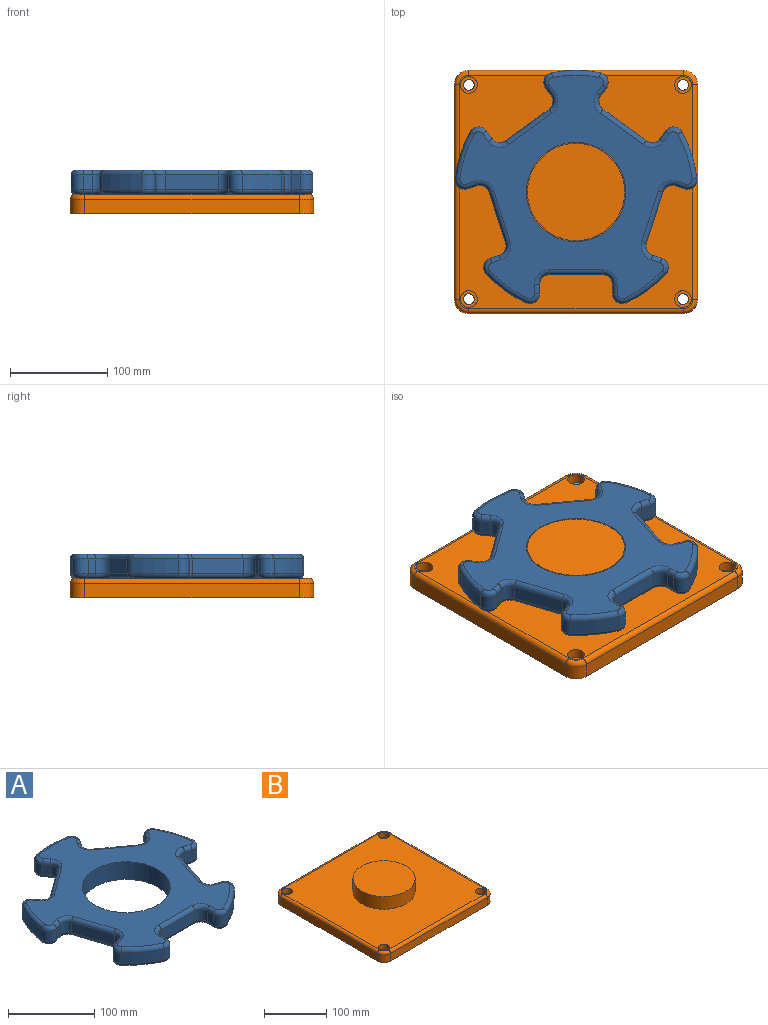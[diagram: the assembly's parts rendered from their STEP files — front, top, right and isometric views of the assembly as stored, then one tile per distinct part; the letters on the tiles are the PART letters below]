
ASSEMBLY  parts=2 mates=1
PART A: 123 faces, bbox 268.9x258.5x25 mm
  f0: plane 238.57x229.73mm, normal (0,0,1), area 21505.7mm2, adj f6,f43,f44,f45,f46,f47,f48,f49
  f1: plane 238.57x229.73mm, normal (0,0,-1), area 21505.7mm2, adj f6,f83,f84,f85,f86,f87,f88,f89
  f2: cylinder r=125mm len=40.68mm, axis (0,0,-1), area 759.5mm2, adj f13,f42,f51,f91
  f3: cylinder r=125mm len=47.82mm, axis (0,0,-1), area 759.5mm2, adj f35,f41,f67,f107
  f4: cylinder r=125mm len=50.29mm, axis (0,0,-1), area 759.5mm2, adj f28,f34,f82,f122
  f5: cylinder r=125mm len=47.82mm, axis (0,0,-1), area 759.5mm2, adj f21,f27,f66,f106
  f6: cylinder r=51mm len=102mm, axis (0,0,-1), area 8011.1mm2, adj f0,f1
  f7: cylinder r=125mm len=40.68mm, axis (0,0,-1), area 759.5mm2, adj f14,f20,f50,f90
  f8: plane 15x9.73mm, normal (-1,0,0), area 146mm2, adj f11,f14,f46,f86
  f9: plane 55x15mm, normal (0,-1,0), area 825mm2, adj f11,f12,f43,f83
  f10: plane 15x9.73mm, normal (1,0,0), area 146mm2, adj f12,f13,f47,f87
  f11: cylinder r=10mm len=15mm, axis (0,0,-1), area 235.6mm2, adj f8,f9,f44,f84
  f12: cylinder r=10mm len=15mm, axis (0,0,-1), area 235.6mm2, adj f9,f10,f45,f85
  f13: cylinder r=10mm len=15mm, axis (0,0,-1), area 299.5mm2, adj f2,f10,f49,f89
  f14: cylinder r=10mm len=15mm, axis (0,0,-1), area 299.5mm2, adj f7,f8,f48,f88
  f15: plane 15x9.26mm, normal (-0.31,-0.95,0), area 146mm2, adj f18,f21,f62,f102
  f16: plane 52.31x17mm, normal (0.95,-0.31,0), area 825mm2, adj f18,f19,f58,f98
  f17: plane 15x9.26mm, normal (0.31,0.95,0), area 146mm2, adj f19,f20,f54,f94
  f18: cylinder r=10mm len=15mm, axis (0,0,-1), area 235.6mm2, adj f15,f16,f60,f100
  f19: cylinder r=10mm len=15mm, axis (0,0,-1), area 235.6mm2, adj f16,f17,f56,f96
  f20: cylinder r=10mm len=16.25mm, axis (0,0,-1), area 299.5mm2, adj f7,f17,f52,f92
  f21: cylinder r=10mm len=15mm, axis (0,0,-1), area 299.5mm2, adj f5,f15,f64,f104
  f22: plane 15x7.87mm, normal (0.81,-0.59,0), area 146mm2, adj f25,f28,f78,f118
  f23: plane 44.5x32.33mm, normal (0.59,0.81,0), area 825mm2, adj f25,f26,f74,f114
  f24: plane 15x7.87mm, normal (-0.81,0.59,0), area 146mm2, adj f26,f27,f70,f110
  f25: cylinder r=10mm len=15mm, axis (0,0,-1), area 235.6mm2, adj f22,f23,f76,f116
  f26: cylinder r=10mm len=15mm, axis (0,0,-1), area 235.6mm2, adj f23,f24,f72,f112
  f27: cylinder r=10mm len=16.78mm, axis (0,0,-1), area 299.5mm2, adj f5,f24,f68,f108
  f28: cylinder r=10mm len=15.67mm, axis (0,0,-1), area 299.5mm2, adj f4,f22,f80,f120
  f29: plane 15x7.87mm, normal (0.81,0.59,0), area 146mm2, adj f32,f35,f71,f111
  f30: plane 44.5x32.33mm, normal (-0.59,0.81,0), area 825mm2, adj f32,f33,f75,f115
  f31: plane 15x7.87mm, normal (-0.81,-0.59,0), area 146mm2, adj f33,f34,f79,f119
  f32: cylinder r=10mm len=15mm, axis (0,0,-1), area 235.6mm2, adj f29,f30,f73,f113
  f33: cylinder r=10mm len=15mm, axis (0,0,-1), area 235.6mm2, adj f30,f31,f77,f117
  f34: cylinder r=10mm len=15.67mm, axis (0,0,-1), area 299.5mm2, adj f4,f31,f81,f121
  f35: cylinder r=10mm len=16.78mm, axis (0,0,-1), area 299.5mm2, adj f3,f29,f69,f109
  f36: plane 15x9.26mm, normal (-0.31,0.95,0), area 146mm2, adj f39,f42,f55,f95
  f37: plane 52.31x17mm, normal (-0.95,-0.31,0), area 825mm2, adj f39,f40,f59,f99
  f38: plane 15x9.26mm, normal (0.31,-0.95,0), area 146mm2, adj f40,f41,f63,f103
  f39: cylinder r=10mm len=15mm, axis (0,0,-1), area 235.6mm2, adj f36,f37,f57,f97
  f40: cylinder r=10mm len=15mm, axis (0,0,-1), area 235.6mm2, adj f37,f38,f61,f101
  f41: cylinder r=10mm len=15mm, axis (0,0,-1), area 299.5mm2, adj f3,f38,f65,f105
  f42: cylinder r=10mm len=16.25mm, axis (0,0,-1), area 299.5mm2, adj f2,f36,f53,f93
  f43: cylinder r=5mm len=55mm, axis (1,0,0), area 432mm2, adj f0,f9,f44,f45
  f44: torus R=15mm, axis (0,0,1), area 145.8mm2, adj f0,f11,f43,f46
  f45: torus R=15mm, axis (0,0,1), area 145.8mm2, adj f0,f12,f43,f47
  f46: cylinder r=5mm len=9.73mm, axis (0,-1,0), area 76.4mm2, adj f0,f8,f44,f48
  f47: cylinder r=5mm len=9.73mm, axis (0,1,0), area 76.4mm2, adj f0,f10,f45,f49
  f48: torus R=5mm, axis (0,0,1), area 128.3mm2, adj f0,f14,f46,f50
  f49: torus R=5mm, axis (0,0,1), area 128.3mm2, adj f0,f13,f47,f51
  f50: torus R=120mm, axis (0,0,1), area 391.9mm2, adj f0,f7,f48,f52
  f51: torus R=120mm, axis (0,0,1), area 391.9mm2, adj f0,f2,f49,f53
  f52: torus R=5mm, axis (0,0,1), area 128.3mm2, adj f0,f20,f50,f54
  f53: torus R=5mm, axis (0,0,1), area 128.3mm2, adj f0,f42,f51,f55
  f54: cylinder r=5mm len=10.8mm, axis (-0.95,0.31,0), area 76.4mm2, adj f0,f17,f52,f56
  f55: cylinder r=5mm len=10.8mm, axis (-0.95,-0.31,0), area 76.4mm2, adj f0,f36,f53,f57
  f56: torus R=15mm, axis (0,0,1), area 145.8mm2, adj f0,f19,f54,f58
  f57: torus R=15mm, axis (0,0,1), area 145.8mm2, adj f0,f39,f55,f59
  f58: cylinder r=5mm len=53.85mm, axis (0.31,0.95,0), area 432mm2, adj f0,f16,f56,f60
  f59: cylinder r=5mm len=53.85mm, axis (0.31,-0.95,0), area 432mm2, adj f0,f37,f57,f61
  f60: torus R=15mm, axis (0,0,1), area 145.8mm2, adj f0,f18,f58,f62
  f61: torus R=15mm, axis (0,0,1), area 145.8mm2, adj f0,f40,f59,f63
  f62: cylinder r=5mm len=10.8mm, axis (0.95,-0.31,0), area 76.4mm2, adj f0,f15,f60,f64
  f63: cylinder r=5mm len=10.8mm, axis (0.95,0.31,0), area 76.4mm2, adj f0,f38,f61,f65
  f64: torus R=5mm, axis (0,0,1), area 128.3mm2, adj f0,f21,f62,f66
  f65: torus R=5mm, axis (0,0,1), area 128.3mm2, adj f0,f41,f63,f67
  f66: torus R=120mm, axis (0,0,1), area 391.9mm2, adj f0,f5,f64,f68
  f67: torus R=120mm, axis (0,0,1), area 391.9mm2, adj f0,f3,f65,f69
  f68: torus R=5mm, axis (0,0,1), area 128.3mm2, adj f0,f27,f66,f70
  f69: torus R=5mm, axis (0,0,1), area 128.3mm2, adj f0,f35,f67,f71
  f70: cylinder r=5mm len=10.81mm, axis (-0.59,-0.81,0), area 76.4mm2, adj f0,f24,f68,f72
  f71: cylinder r=5mm len=10.81mm, axis (-0.59,0.81,0), area 76.4mm2, adj f0,f29,f69,f73
  f72: torus R=15mm, axis (0,0,1), area 145.8mm2, adj f0,f26,f70,f74
  f73: torus R=15mm, axis (0,0,1), area 145.8mm2, adj f0,f32,f71,f75
  f74: cylinder r=5mm len=47.44mm, axis (-0.81,0.59,0), area 432mm2, adj f0,f23,f72,f76
  f75: cylinder r=5mm len=47.44mm, axis (-0.81,-0.59,0), area 432mm2, adj f0,f30,f73,f77
  f76: torus R=15mm, axis (0,0,1), area 145.8mm2, adj f0,f25,f74,f78
  f77: torus R=15mm, axis (0,0,1), area 145.8mm2, adj f0,f33,f75,f79
  f78: cylinder r=5mm len=10.81mm, axis (0.59,0.81,0), area 76.4mm2, adj f0,f22,f76,f80
  f79: cylinder r=5mm len=10.81mm, axis (0.59,-0.81,0), area 76.4mm2, adj f0,f31,f77,f81
  f80: torus R=5mm, axis (0,0,1), area 128.3mm2, adj f0,f28,f78,f82
  f81: torus R=5mm, axis (0,0,1), area 128.3mm2, adj f0,f34,f79,f82
  f82: torus R=120mm, axis (0,0,1), area 391.9mm2, adj f0,f4,f80,f81
  f83: cylinder r=5mm len=55mm, axis (-1,0,0), area 432mm2, adj f1,f9,f84,f85
  f84: torus R=15mm, axis (0,0,1), area 145.8mm2, adj f1,f11,f83,f86
  f85: torus R=15mm, axis (0,0,1), area 145.8mm2, adj f1,f12,f83,f87
  f86: cylinder r=5mm len=9.73mm, axis (0,1,0), area 76.4mm2, adj f1,f8,f84,f88
  f87: cylinder r=5mm len=9.73mm, axis (0,-1,0), area 76.4mm2, adj f1,f10,f85,f89
  f88: torus R=5mm, axis (0,0,1), area 128.3mm2, adj f1,f14,f86,f90
  f89: torus R=5mm, axis (0,0,1), area 128.3mm2, adj f1,f13,f87,f91
  f90: torus R=120mm, axis (0,0,1), area 391.9mm2, adj f1,f7,f88,f92
  f91: torus R=120mm, axis (0,0,1), area 391.9mm2, adj f1,f2,f89,f93
  f92: torus R=5mm, axis (0,0,1), area 128.3mm2, adj f1,f20,f90,f94
  f93: torus R=5mm, axis (0,0,1), area 128.3mm2, adj f1,f42,f91,f95
  f94: cylinder r=5mm len=10.8mm, axis (0.95,-0.31,0), area 76.4mm2, adj f1,f17,f92,f96
  f95: cylinder r=5mm len=10.8mm, axis (0.95,0.31,0), area 76.4mm2, adj f1,f36,f93,f97
  f96: torus R=15mm, axis (0,0,1), area 145.8mm2, adj f1,f19,f94,f98
  f97: torus R=15mm, axis (0,0,1), area 145.8mm2, adj f1,f39,f95,f99
  f98: cylinder r=5mm len=53.85mm, axis (-0.31,-0.95,0), area 432mm2, adj f1,f16,f96,f100
  f99: cylinder r=5mm len=53.85mm, axis (-0.31,0.95,0), area 432mm2, adj f1,f37,f97,f101
  f100: torus R=15mm, axis (0,0,1), area 145.8mm2, adj f1,f18,f98,f102
  f101: torus R=15mm, axis (0,0,1), area 145.8mm2, adj f1,f40,f99,f103
  f102: cylinder r=5mm len=10.8mm, axis (-0.95,0.31,0), area 76.4mm2, adj f1,f15,f100,f104
  f103: cylinder r=5mm len=10.8mm, axis (-0.95,-0.31,0), area 76.4mm2, adj f1,f38,f101,f105
  f104: torus R=5mm, axis (0,0,1), area 128.3mm2, adj f1,f21,f102,f106
  f105: torus R=5mm, axis (0,0,1), area 128.3mm2, adj f1,f41,f103,f107
  f106: torus R=120mm, axis (0,0,1), area 391.9mm2, adj f1,f5,f104,f108
  f107: torus R=120mm, axis (0,0,1), area 391.9mm2, adj f1,f3,f105,f109
  f108: torus R=5mm, axis (0,0,1), area 128.3mm2, adj f1,f27,f106,f110
  f109: torus R=5mm, axis (0,0,1), area 128.3mm2, adj f1,f35,f107,f111
  f110: cylinder r=5mm len=10.81mm, axis (0.59,0.81,0), area 76.4mm2, adj f1,f24,f108,f112
  f111: cylinder r=5mm len=10.81mm, axis (0.59,-0.81,0), area 76.4mm2, adj f1,f29,f109,f113
  f112: torus R=15mm, axis (0,0,1), area 145.8mm2, adj f1,f26,f110,f114
  f113: torus R=15mm, axis (0,0,1), area 145.8mm2, adj f1,f32,f111,f115
  f114: cylinder r=5mm len=47.44mm, axis (0.81,-0.59,0), area 432mm2, adj f1,f23,f112,f116
  f115: cylinder r=5mm len=47.44mm, axis (0.81,0.59,0), area 432mm2, adj f1,f30,f113,f117
  f116: torus R=15mm, axis (0,0,1), area 145.8mm2, adj f1,f25,f114,f118
  f117: torus R=15mm, axis (0,0,1), area 145.8mm2, adj f1,f33,f115,f119
  f118: cylinder r=5mm len=10.81mm, axis (-0.59,-0.81,0), area 76.4mm2, adj f1,f22,f116,f120
  f119: cylinder r=5mm len=10.81mm, axis (-0.59,0.81,0), area 76.4mm2, adj f1,f31,f117,f121
  f120: torus R=5mm, axis (0,0,1), area 128.3mm2, adj f1,f28,f118,f122
  f121: torus R=5mm, axis (0,0,1), area 128.3mm2, adj f1,f34,f119,f122
  f122: torus R=120mm, axis (0,0,1), area 391.9mm2, adj f1,f4,f120,f121
PART B: 32 faces, bbox 252.5x252.5x45 mm
  f0: plane 220x15mm, normal (1,0,0), area 3300mm2, adj f5,f8,f11,f27
  f1: plane 220x15mm, normal (0,1,0), area 3300mm2, adj f5,f8,f9,f31
  f2: plane 220x15mm, normal (-1,0,0), area 3300mm2, adj f5,f9,f10,f28
  f3: plane 220x15mm, normal (0,-1,0), area 3300mm2, adj f5,f10,f11,f24
  f4: plane 240x240mm, normal (0,0,1), area 48725.4mm2, adj f6,f14,f17,f20,f23,f24,f25,f26
  f5: plane 250x250mm, normal (0,0,-1), area 61926.7mm2, adj f0,f1,f2,f3,f8,f9,f10,f11
  f6: cylinder r=50mm len=100mm, axis (0,0,-1), area 7854mm2, adj f4,f7
  f7: plane 100x100mm, normal (0,0,1), area 7854mm2, adj f6
  f8: cylinder r=15mm len=15mm, axis (0,0,-1), area 353.4mm2, adj f0,f1,f5,f29
  f9: cylinder r=15mm len=15mm, axis (0,0,1), area 353.4mm2, adj f1,f2,f5,f30
  f10: cylinder r=15mm len=15mm, axis (0,0,-1), area 353.4mm2, adj f2,f3,f5,f26
  f11: cylinder r=15mm len=15mm, axis (0,0,1), area 353.4mm2, adj f0,f3,f5,f25
  f12: cylinder r=5.5mm len=11mm, axis (0,0,1), area 345.6mm2, adj f5,f13
  f13: plane 17.25x17.25mm, normal (0,0,1), area 138.7mm2, adj f12,f14
  f14: cylinder r=8.62mm len=17.25mm, axis (0,0,1), area 541.9mm2, adj f4,f13
  f15: cylinder r=5.5mm len=11mm, axis (0,0,1), area 345.6mm2, adj f5,f16
  f16: plane 17.25x17.25mm, normal (0,0,1), area 138.7mm2, adj f15,f17
  f17: cylinder r=8.62mm len=17.25mm, axis (0,0,1), area 541.9mm2, adj f4,f16
  f18: cylinder r=5.5mm len=11mm, axis (0,0,1), area 345.6mm2, adj f5,f19
  f19: plane 17.25x17.25mm, normal (0,0,1), area 138.7mm2, adj f18,f20
  f20: cylinder r=8.62mm len=17.25mm, axis (0,0,1), area 541.9mm2, adj f4,f19
  f21: cylinder r=5.5mm len=11mm, axis (0,0,1), area 345.6mm2, adj f5,f22
  f22: plane 17.25x17.25mm, normal (0,0,1), area 138.7mm2, adj f21,f23
  f23: cylinder r=8.62mm len=17.25mm, axis (0,0,1), area 541.9mm2, adj f4,f22
  f24: cylinder r=5mm len=220mm, axis (-1,0,0), area 1727.9mm2, adj f3,f4,f25,f26
  f25: torus R=10mm, axis (0,0,1), area 162.6mm2, adj f4,f11,f24,f27
  f26: torus R=10mm, axis (0,0,1), area 162.6mm2, adj f4,f10,f24,f28
  f27: cylinder r=5mm len=220mm, axis (0,-1,0), area 1727.9mm2, adj f0,f4,f25,f29
  f28: cylinder r=5mm len=220mm, axis (0,1,0), area 1727.9mm2, adj f2,f4,f26,f30
  f29: torus R=10mm, axis (0,0,1), area 162.6mm2, adj f4,f8,f27,f31
  f30: torus R=10mm, axis (0,0,1), area 162.6mm2, adj f4,f9,f28,f31
  f31: cylinder r=5mm len=220mm, axis (1,0,0), area 1727.9mm2, adj f1,f4,f29,f30
PLACE A t=(-53.72,21.39,4.64)mm
PLACE B t=(-53.72,21.39,4.64)mm
MATE revolute A.f2 <-> B.f6  axis (0,0,1) through (-53.72,21.39,49.64)mm
